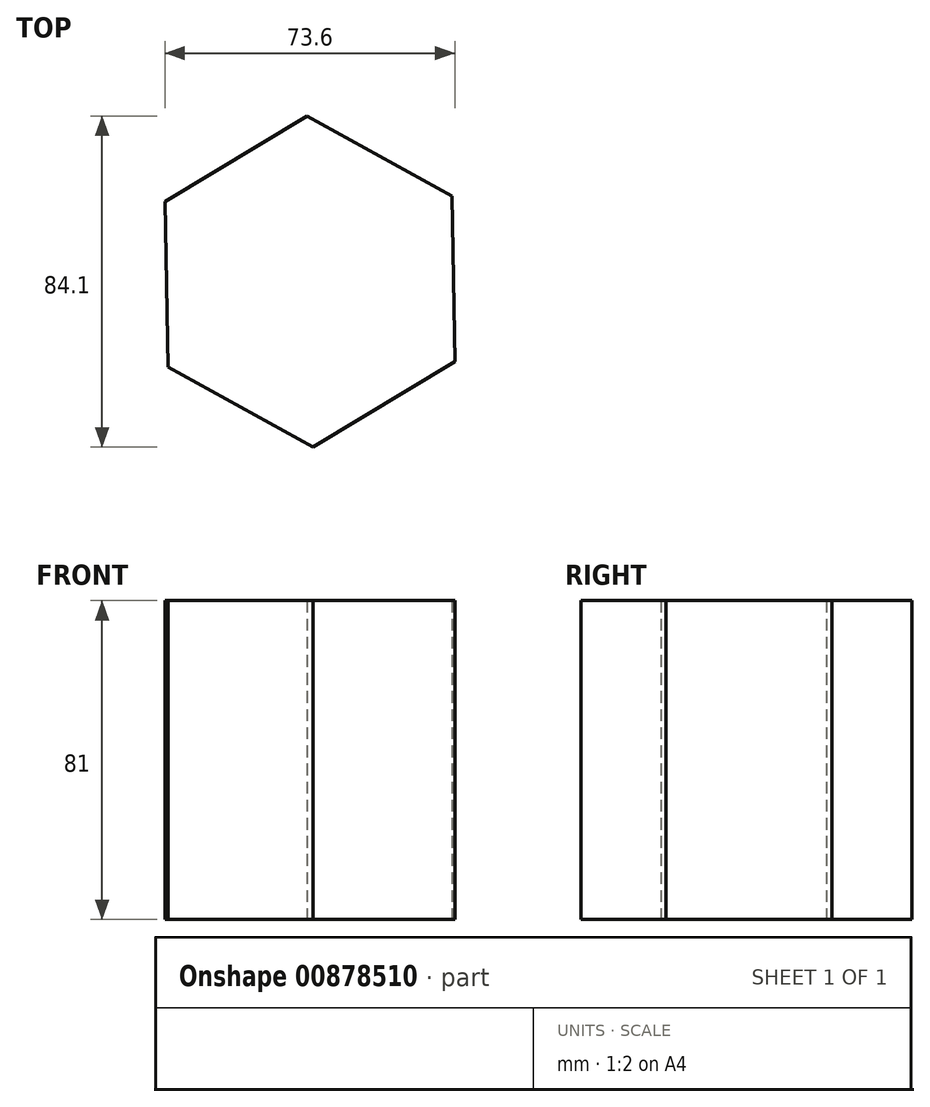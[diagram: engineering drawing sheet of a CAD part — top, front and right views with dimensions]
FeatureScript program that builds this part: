
annotation { "Feature Type Name" : "Feature", "Feature Type Description" : "" }
export const myFeature = defineFeature(function(context is Context, id is Id, definition is map)
    precondition{}
    {
        {
            var Q0;
            Q0=qCreatedBy(makeId("Top.planeOp"),FACE);
            var sketch = newSketch(context, id + "F0", { "sketchPlane" : qUnion([Q0])});
            skCircle(sketch, "E0.cCircle", {"center": v(0, 0) * mm, "radius": 36.43 * mm, "construction": true});
            skLineSegment(sketch, "E0.0", {"start": v(-36.8, 20.37) * mm, "end": v(-0.76, 42.05) * mm});
            skLineSegment(sketch, "E0.1", {"start": v(-0.76, 42.05) * mm, "end": v(36.04, 21.69) * mm});
            skLineSegment(sketch, "E0.2", {"start": v(36.04, 21.69) * mm, "end": v(36.8, -20.37) * mm});
            skLineSegment(sketch, "E0.3", {"start": v(36.8, -20.37) * mm, "end": v(0.76, -42.05) * mm});
            skLineSegment(sketch, "E0.4", {"start": v(0.76, -42.05) * mm, "end": v(-36.04, -21.69) * mm});
            skLineSegment(sketch, "E0.5", {"start": v(-36.04, -21.69) * mm, "end": v(-36.8, 20.37) * mm});
            skPoint(sketch, "E0.0.midPoint", {"position": v(-18.78, 31.21) * mm});
            skSolve(sketch);
        }
        {
            var Q0;
            Q0=makeQuery(id+"F0.imprint","IMPRINT",FACE,{"disambiguationData":[TD([[makeQuery(id+"F0.imprint","IMPRINT",EDGE,{"derivedFrom":sQuery(id+"F0.wireOp",EDGE,"E0.0")}),-1.0]])]});
            extrude(context, id + "F1", {"entities" : qUnion([Q0]), "depth" : 81 * mm, "offsetDistance" : 25 * mm});
        }
    });
